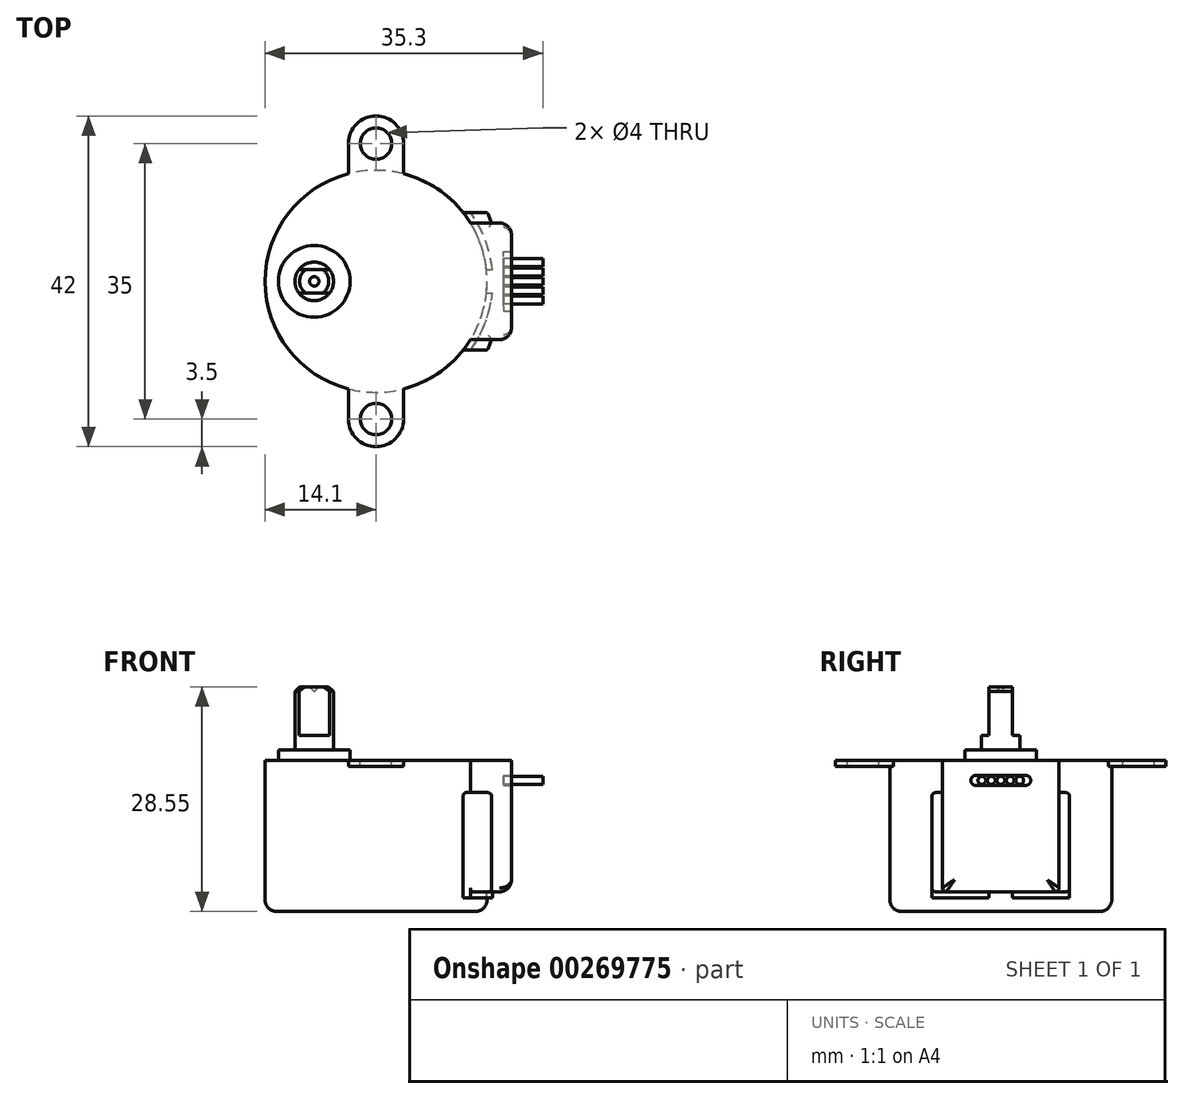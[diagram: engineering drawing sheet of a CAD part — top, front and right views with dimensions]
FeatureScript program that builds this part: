
annotation { "Feature Type Name" : "Feature", "Feature Type Description" : "" }
export const myFeature = defineFeature(function(context is Context, id is Id, definition is map)
    precondition{}
    {
        {
            var Q0;
            Q0=qCreatedBy(makeId("Front.planeOp"),FACE);
            var sketch = newSketch(context, id + "F0", { "sketchPlane" : qUnion([Q0])});
            skLineSegment(sketch, "E0", {"start": v(0, 0) * mm, "end": v(0, 8.75) * mm});
            skLineSegment(sketch, "E1", {"start": v(0.6, 9.35) * mm, "end": v(1.85, 9.35) * mm});
            skLineSegment(sketch, "E2", {"start": v(2.45, 8.75) * mm, "end": v(2.45, 1.35) * mm});
            skLineSegment(sketch, "E3", {"start": v(2.45, 1.35) * mm, "end": v(4.55, 1.35) * mm});
            skLineSegment(sketch, "E4", {"start": v(4.55, 1.35) * mm, "end": v(4.55, 0) * mm});
            skLineSegment(sketch, "E5", {"start": v(4.55, 0) * mm, "end": v(0, 0) * mm});
            skLineSegment(sketch, "E6", {"start": v(1.85, 9.35) * mm, "end": v(2.45, 8.75) * mm});
            skLineSegment(sketch, "E7", {"start": v(0.6, 9.35) * mm, "end": v(0, 8.75) * mm});
            skLineSegment(sketch, "E8", {"start": v(0, 8.75) * mm, "end": v(0, 13.35) * mm, "construction": true});
            skSolve(sketch);
        }
        {
            var Q0;
            Q0=makeQuery(id+"F0.imprint","IMPRINT",FACE,{"disambiguationData":[TD([[makeQuery(id+"F0.imprint","IMPRINT",EDGE,{"derivedFrom":sQuery(id+"F0.wireOp",EDGE,"E0")}),-1.0]])]});
            var Q1;
            Q1=sQuery(id+"F0.wireOp",EDGE,"E8");
            revolve(context, id + "F1", {"entities" : qUnion([Q0]), "axis" : qUnion([Q1]), "revolveType" : RevolveType.FULL});
        }
        {
            var Q0;
            Q0=makeQuery(id+"F1.opRevolve","SWEPT_FACE",FACE,{"disambiguationData":[OSD([sQuery(id+"F0.wireOp",EDGE,"E1")])]});
            var sketch = newSketch(context, id + "F2", { "sketchPlane" : qUnion([Q0])});
            skLineSegment(sketch, "E9", {"start": v(-3.37, 1.5) * mm, "end": v(3.8, 1.5) * mm});
            skLineSegment(sketch, "E10", {"start": v(3.8, 1.5) * mm, "end": v(3.8, 4.5) * mm});
            skLineSegment(sketch, "E11", {"start": v(3.8, 4.5) * mm, "end": v(-3.37, 4.5) * mm});
            skLineSegment(sketch, "E12", {"start": v(-3.37, 4.5) * mm, "end": v(-3.37, 1.5) * mm});
            skLineSegment(sketch, "E13", {"start": v(0, 0) * mm, "end": v(9.16, 0) * mm, "construction": true});
            skLineSegment(sketch, "E14.MirrorCS", {"start": v(-3.37, -4.5) * mm, "end": v(-3.37, -1.5) * mm});
            skLineSegment(sketch, "E15.MirrorCS", {"start": v(3.8, -4.5) * mm, "end": v(-3.37, -4.5) * mm});
            skLineSegment(sketch, "E16.MirrorCS", {"start": v(3.8, -1.5) * mm, "end": v(3.8, -4.5) * mm});
            skLineSegment(sketch, "E17.MirrorCS", {"start": v(-3.37, -1.5) * mm, "end": v(3.8, -1.5) * mm});
            skSolve(sketch);
        }
        {
            var Q0;
            Q0=qSketchRegion(id+"F2",true);
            extrude(context, id + "F3", {"entities" : qUnion([Q0]), "operationType" : NewBodyOperationType.REMOVE, "oppositeDirection" : true, "depth" : 6.2 * mm});
        }
        {
            var Q0;
            Q0=makeQuery(id+"F1.opRevolve","SWEPT_FACE",FACE,{"disambiguationData":[OSD([sQuery(id+"F0.wireOp",EDGE,"E5")])]});
            var sketch = newSketch(context, id + "F4", { "sketchPlane" : qUnion([Q0])});
            skLineSegment(sketch, "E18", {"start": v(0, 0) * mm, "end": v(7.85, 0) * mm, "construction": true});
            skCircle(sketch, "E19", {"center": v(7.85, 0) * mm, "radius": 14.1 * mm});
            skLineSegment(sketch, "E20", {"start": v(0, 0) * mm, "end": v(-4.55, 0) * mm, "construction": true});
            skLineSegment(sketch, "E21", {"start": v(-4.55, 0) * mm, "end": v(-6.25, 0) * mm, "construction": true});
            skSolve(sketch);
        }
        {
            var Q0;
            Q0=qSketchRegion(id+"F4",true);
            extrude(context, id + "F5", {"entities" : qUnion([Q0]), "depth" : 19.2 * mm});
        }
        {
            var Q0;
            Q0=makeQuery(id+"F5.opExtrude","CAP_FACE",FACE,{"disambiguationData":[OSD([sQuery(id+"F0.wireOp",EDGE,"E4"),sQuery(id+"F0.wireOp",EDGE,"E5"),sQuery(id+"F4.wireOp",EDGE,"E19")])],"isStart":true});
            var sketch = newSketch(context, id + "F6", { "sketchPlane" : qUnion([Q0])});
            skLineSegment(sketch, "E22", {"start": v(7.85, 0) * mm, "end": v(7.85, 17.5) * mm, "construction": true});
            skCircle(sketch, "E23", {"center": v(7.85, 17.5) * mm, "radius": 2 * mm});
            skArc(sketch, "E24", {"start": v(11.35, 17.5) * mm, "mid": v(7.85, 21) * mm, "end": v(4.35, 17.5) * mm});
            skLineSegment(sketch, "E25", {"start": v(7.85, 0) * mm, "end": v(11.35, 0) * mm, "construction": true});
            skLineSegment(sketch, "E26", {"start": v(11.35, 0) * mm, "end": v(11.35, 17.5) * mm});
            skLineSegment(sketch, "E27", {"start": v(7.85, 0) * mm, "end": v(4.35, 0) * mm, "construction": true});
            skLineSegment(sketch, "E28", {"start": v(4.35, 0) * mm, "end": v(4.35, 17.5) * mm});
            skLineSegment(sketch, "E29.MirrorCS", {"start": v(4.35, 0) * mm, "end": v(4.35, -17.5) * mm});
            skArc(sketch, "E30.MirrorCS", {"start": v(11.35, -17.5) * mm, "mid": v(7.85, -21) * mm, "end": v(4.35, -17.5) * mm});
            skCircle(sketch, "E31.MirrorC", {"center": v(7.85, -17.5) * mm, "radius": 2 * mm});
            skLineSegment(sketch, "E32.MirrorCS", {"start": v(11.35, 0) * mm, "end": v(11.35, -17.5) * mm});
            skSolve(sketch);
        }
        {
            var Q0;
            Q0=qSketchRegion(id+"F6",true);
            extrude(context, id + "F7", {"entities" : qUnion([Q0]), "oppositeDirection" : true, "depth" : 0.75 * mm});
        }
        {
            var Q0;
            Q0=makeQuery(id+"F7.opExtrude","SWEPT_BODY",BODY,{"disambiguationData":[OSD([sQuery(id+"F6.wireOp",EDGE,"E23"),sQuery(id+"F6.wireOp",EDGE,"E24"),sQuery(id+"F6.wireOp",EDGE,"E26"),sQuery(id+"F6.wireOp",EDGE,"E28"),sQuery(id+"F6.wireOp",EDGE,"E29.MirrorCS"),sQuery(id+"F6.wireOp",EDGE,"E32.MirrorCS"),sQuery(id+"F6.wireOp",EDGE,"E30.MirrorCS"),sQuery(id+"F6.wireOp",EDGE,"E31.MirrorC")])]});
            var Q1;
            Q1=makeQuery(id+"F5.opExtrude","SWEPT_BODY",BODY,{"disambiguationData":[OSD([sQuery(id+"F0.wireOp",EDGE,"E4"),sQuery(id+"F0.wireOp",EDGE,"E5"),sQuery(id+"F4.wireOp",EDGE,"E19")])]});
            booleanBodies(context, id + "F8", {"operationType" : BooleanOperationType.UNION, "tools" : qUnion([Q0, Q1])});
        }
        {
            var Q0;
            Q0=makeQuery(id+"F8.opBoolean","MERGE",FACE,{"derivedFrom":[makeQuery(id+"F5.opExtrude","CAP_FACE",FACE,{"disambiguationData":[OSD([sQuery(id+"F4.wireOp",EDGE,"E19")])],"isStart":true}),makeQuery(id+"F7.opExtrude","CAP_FACE",FACE,{"disambiguationData":[OSD([sQuery(id+"F6.wireOp",EDGE,"E23"),sQuery(id+"F6.wireOp",EDGE,"E24"),sQuery(id+"F6.wireOp",EDGE,"E26"),sQuery(id+"F6.wireOp",EDGE,"E28"),sQuery(id+"F6.wireOp",EDGE,"E29.MirrorCS"),sQuery(id+"F6.wireOp",EDGE,"E32.MirrorCS"),sQuery(id+"F6.wireOp",EDGE,"E30.MirrorCS"),sQuery(id+"F6.wireOp",EDGE,"E31.MirrorC")])],"isStart":true})]});
            var sketch = newSketch(context, id + "F9", { "sketchPlane" : qUnion([Q0])});
            skLineSegment(sketch, "E33", {"start": v(7.85, 0) * mm, "end": v(25.05, 0) * mm, "construction": true});
            skPoint(sketch, "E33.endSnap0", {"position": v(21.95, 0) * mm});
            skLineSegment(sketch, "E34", {"start": v(25.05, 0) * mm, "end": v(25.05, 7.4) * mm});
            skLineSegment(sketch, "E35", {"start": v(25.05, 7.4) * mm, "end": v(7.85, 7.4) * mm});
            skLineSegment(sketch, "E36", {"start": v(7.85, 7.4) * mm, "end": v(7.85, 0) * mm});
            skLineSegment(sketch, "E37.MirrorCS", {"start": v(7.85, -7.4) * mm, "end": v(7.85, 0) * mm});
            skLineSegment(sketch, "E38.MirrorCS", {"start": v(25.05, -7.4) * mm, "end": v(7.85, -7.4) * mm});
            skLineSegment(sketch, "E39.MirrorCS", {"start": v(25.05, 0) * mm, "end": v(25.05, -7.4) * mm});
            skSolve(sketch);
        }
        {
            var Q0;
            {var subQ1=sQuery(id+"F9.wireOp",EDGE,"E34");Q0=makeQuery(id+"F9.imprint","IMPRINT",FACE,{"disambiguationData":[TD([[makeQuery(id+"F9.imprint","IMPRINT",EDGE,{"derivedFrom":subQ1}),1.0]])]});}
            extrude(context, id + "F10", {"entities" : qUnion([Q0]), "operationType" : NewBodyOperationType.ADD, "oppositeDirection" : true, "depth" : 16.7 * mm});
        }
        {
            var Q0;
            Q0=makeQuery(id+"F10.opExtrude","CAP_FACE",FACE,{"disambiguationData":[OSD([sQuery(id+"F4.wireOp",EDGE,"E19"),sQuery(id+"F9.wireOp",EDGE,"E34"),sQuery(id+"F9.wireOp",EDGE,"E35"),sQuery(id+"F9.wireOp",EDGE,"E38.MirrorCS"),sQuery(id+"F9.wireOp",EDGE,"E39.MirrorCS")])],"isStart":false});
            var sketch = newSketch(context, id + "F11", { "sketchPlane" : qUnion([Q0])});
            skLineSegment(sketch, "E40", {"start": v(25.05, 0) * mm, "end": v(21.95, 0) * mm, "construction": true});
            skLineSegment(sketch, "E41", {"start": v(22.55, 0) * mm, "end": v(22.55, 7.4) * mm});
            skLineSegment(sketch, "E42", {"start": v(22.55, 7.4) * mm, "end": v(22.05, 8.75) * mm});
            skLineSegment(sketch, "E43", {"start": v(22.05, 8.75) * mm, "end": v(18.9, 8.75) * mm});
            skLineSegment(sketch, "E44", {"start": v(18.9, 8.75) * mm, "end": v(18.9, 0) * mm});
            skLineSegment(sketch, "E45.MirrorCS", {"start": v(22.55, 0) * mm, "end": v(22.55, -7.4) * mm});
            skLineSegment(sketch, "E46.MirrorCS", {"start": v(22.55, -7.4) * mm, "end": v(22.05, -8.75) * mm});
            skLineSegment(sketch, "E47.MirrorCS", {"start": v(22.05, -8.75) * mm, "end": v(18.9, -8.75) * mm});
            skLineSegment(sketch, "E48.MirrorCS", {"start": v(18.9, -8.75) * mm, "end": v(18.9, 0) * mm});
            skSolve(sketch);
        }
        {
            var Q0;
            {var subQ3=sQuery(id+"F11.wireOp",EDGE,"E42");Q0=makeQuery(id+"F11.imprint","IMPRINT",FACE,{"disambiguationData":[TD([[makeQuery(id+"F11.imprint","IMPRINT",EDGE,{"derivedFrom":subQ3}),1.0]])]});}
            var Q1;
            {var subQ3=sQuery(id+"F11.wireOp",EDGE,"E41");Q1=makeQuery(id+"F11.imprint","IMPRINT",FACE,{"disambiguationData":[TD([[makeQuery(id+"F11.imprint","IMPRINT",EDGE,{"derivedFrom":subQ3}),1.0]])]});}
            extrude(context, id + "F12", {"entities" : qUnion([Q0, Q1]), "operationType" : NewBodyOperationType.ADD, "oppositeDirection" : true, "depth" : 12.6 * mm});
        }
        {
            var Q0;
            Q0=makeQuery(id+"F12.boolean.opBoolean","MERGE",FACE,{"derivedFrom":[makeQuery(id+"F10.opExtrude","CAP_FACE",FACE,{"disambiguationData":[OSD([sQuery(id+"F4.wireOp",EDGE,"E19"),sQuery(id+"F9.wireOp",EDGE,"E34"),sQuery(id+"F9.wireOp",EDGE,"E35"),sQuery(id+"F9.wireOp",EDGE,"E38.MirrorCS"),sQuery(id+"F9.wireOp",EDGE,"E39.MirrorCS")])],"isStart":false}),makeQuery(id+"F12.opExtrude","CAP_FACE",FACE,{"disambiguationData":[OSD([sQuery(id+"F11.wireOp",EDGE,"E41"),sQuery(id+"F11.wireOp",EDGE,"E42"),sQuery(id+"F11.wireOp",EDGE,"E43"),sQuery(id+"F11.wireOp",EDGE,"E44"),sQuery(id+"F11.wireOp",EDGE,"E45.MirrorCS"),sQuery(id+"F11.wireOp",EDGE,"E46.MirrorCS"),sQuery(id+"F11.wireOp",EDGE,"E47.MirrorCS"),sQuery(id+"F11.wireOp",EDGE,"E48.MirrorCS")])],"isStart":true})]});
            var sketch = newSketch(context, id + "F13", { "sketchPlane" : qUnion([Q0])});
            skLineSegment(sketch, "E49", {"start": v(25.05, 0) * mm, "end": v(7.85, 0) * mm, "construction": true});
            skArc(sketch, "E50", {"start": v(18.9, -8.75) * mm, "mid": v(20.9, -5.33) * mm, "end": v(21.87, -1.5) * mm});
            skArc(sketch, "E51", {"start": v(19.84, -8.75) * mm, "mid": v(21.71, -5.3) * mm, "end": v(22.62, -1.5) * mm});
            skLineSegment(sketch, "E52", {"start": v(18.9, -8.75) * mm, "end": v(19.84, -8.75) * mm});
            skLineSegment(sketch, "E53", {"start": v(21.87, -1.5) * mm, "end": v(22.62, -1.5) * mm});
            skLineSegment(sketch, "E54.MirrorCS", {"start": v(21.87, 1.5) * mm, "end": v(22.62, 1.5) * mm});
            skArc(sketch, "E55.MirrorCS", {"start": v(19.84, 8.75) * mm, "mid": v(21.71, 5.3) * mm, "end": v(22.62, 1.5) * mm});
            skArc(sketch, "E56.MirrorCS", {"start": v(18.9, 8.75) * mm, "mid": v(20.9, 5.33) * mm, "end": v(21.87, 1.5) * mm});
            skLineSegment(sketch, "E57.MirrorCS", {"start": v(18.9, 8.75) * mm, "end": v(19.84, 8.75) * mm});
            skSolve(sketch);
        }
        {
            var Q0;
            Q0=makeQuery(id+"F13.imprint","IMPRINT",FACE,{"disambiguationData":[TD([[makeQuery(id+"F13.imprint","IMPRINT",EDGE,{"derivedFrom":sQuery(id+"F13.wireOp",EDGE,"E50")}),-1.0]])]});
            var Q1;
            Q1=makeQuery(id+"F13.imprint","IMPRINT",FACE,{"disambiguationData":[TD([[makeQuery(id+"F13.imprint","IMPRINT",EDGE,{"derivedFrom":sQuery(id+"F13.wireOp",EDGE,"E54.MirrorCS")}),1.0]])]});
            extrude(context, id + "F14", {"entities" : qUnion([Q0, Q1]), "operationType" : NewBodyOperationType.ADD, "depth" : 0.75 * mm});
        }
        {
            var Q0;
            Q0=makeQuery(id+"F10.opExtrude","SWEPT_EDGE",EDGE,{"disambiguationData":[OSD([sQuery(id+"F9.wireOp",EDGE,"E38.MirrorCS"),sQuery(id+"F9.wireOp",EDGE,"E39.MirrorCS")])]});
            var Q1;
            Q1=makeQuery(id+"F10.opExtrude","SWEPT_EDGE",EDGE,{"disambiguationData":[OSD([sQuery(id+"F9.wireOp",EDGE,"E34"),sQuery(id+"F9.wireOp",EDGE,"E35")])]});
            var Q2;
            Q2=makeQuery(id+"F10.opExtrude","CAP_EDGE",EDGE,{"disambiguationData":[OSD([sQuery(id+"F9.wireOp",EDGE,"E34"),sQuery(id+"F9.wireOp",EDGE,"E39.MirrorCS")])],"isStart":false});
            var Q3;
            Q3=makeQuery(id+"F5.opExtrude","CAP_EDGE",EDGE,{"disambiguationData":[OSD([sQuery(id+"F4.wireOp",EDGE,"E19")])],"isStart":false});
            fillet(context, id + "F15", {"entities" : qUnion([Q0, Q1, Q2, Q3]), "radius" : 1.5 * mm, "tangentPropagation" : true, "allowEdgeOverflow" : false});
        }
        {
            var Q0;
            Q0=makeQuery(id+"F10.opExtrude","CAP_EDGE",EDGE,{"disambiguationData":[OSD([sQuery(id+"F9.wireOp",EDGE,"E35")])],"isStart":false});
            var Q1;
            Q1=makeQuery(id+"F12.opExtrude","CAP_EDGE",EDGE,{"disambiguationData":[OSD([sQuery(id+"F11.wireOp",EDGE,"E46.MirrorCS")])],"isStart":true});
            var Q2;
            Q2=makeQuery(id+"F12.opExtrude","CAP_EDGE",EDGE,{"disambiguationData":[OSD([sQuery(id+"F11.wireOp",EDGE,"E47.MirrorCS")])],"isStart":true});
            var Q3;
            Q3=makeQuery(id+"F12.opExtrude","SWEPT_EDGE",EDGE,{"disambiguationData":[OSD([sQuery(id+"F11.wireOp",EDGE,"E46.MirrorCS"),sQuery(id+"F11.wireOp",EDGE,"E47.MirrorCS")])]});
            var Q4;
            Q4=makeQuery(id+"F12.opExtrude","CAP_EDGE",EDGE,{"disambiguationData":[OSD([sQuery(id+"F11.wireOp",EDGE,"E46.MirrorCS")])],"isStart":false});
            var Q5;
            Q5=makeQuery(id+"F12.opExtrude","CAP_EDGE",EDGE,{"disambiguationData":[OSD([sQuery(id+"F11.wireOp",EDGE,"E47.MirrorCS")])],"isStart":false});
            var Q6;
            Q6=makeQuery(id+"F10.opExtrude","CAP_EDGE",EDGE,{"disambiguationData":[OSD([sQuery(id+"F9.wireOp",EDGE,"E38.MirrorCS")])],"isStart":false});
            var Q7;
            Q7=makeQuery(id+"F12.opExtrude","CAP_EDGE",EDGE,{"disambiguationData":[OSD([sQuery(id+"F11.wireOp",EDGE,"E42")])],"isStart":true});
            var Q8;
            Q8=makeQuery(id+"F12.opExtrude","CAP_EDGE",EDGE,{"disambiguationData":[OSD([sQuery(id+"F11.wireOp",EDGE,"E43")])],"isStart":true});
            var Q9;
            Q9=makeQuery(id+"F12.opExtrude","SWEPT_EDGE",EDGE,{"disambiguationData":[OSD([sQuery(id+"F11.wireOp",EDGE,"E42"),sQuery(id+"F11.wireOp",EDGE,"E43")])]});
            var Q10;
            Q10=makeQuery(id+"F12.opExtrude","CAP_EDGE",EDGE,{"disambiguationData":[OSD([sQuery(id+"F11.wireOp",EDGE,"E42")])],"isStart":false});
            var Q11;
            Q11=makeQuery(id+"F12.opExtrude","CAP_EDGE",EDGE,{"disambiguationData":[OSD([sQuery(id+"F11.wireOp",EDGE,"E43")])],"isStart":false});
            fillet(context, id + "F16", {"entities" : qUnion([Q0, Q1, Q2, Q3, Q4, Q5, Q6, Q7, Q8, Q9, Q10, Q11]), "radius" : 0.5 * mm, "tangentPropagation" : true, "allowEdgeOverflow" : false});
        }
        {
            var Q0;
            Q0=makeQuery(id+"F10.opExtrude","SWEPT_FACE",FACE,{"disambiguationData":[OSD([sQuery(id+"F9.wireOp",EDGE,"E34"),sQuery(id+"F9.wireOp",EDGE,"E39.MirrorCS")])]});
            var sketch = newSketch(context, id + "F17", { "sketchPlane" : qUnion([Q0])});
            skLineSegment(sketch, "E58", {"start": v(0, 0) * mm, "end": v(0, -2.55) * mm, "construction": true});
            skLineSegment(sketch, "E59", {"start": v(0, -2.55) * mm, "end": v(-3.15, -2.55) * mm, "construction": true});
            skArc(sketch, "E60", {"start": v(-3.15, -1.9) * mm, "mid": v(-3.8, -2.55) * mm, "end": v(-3.15, -3.2) * mm});
            skLineSegment(sketch, "E61", {"start": v(-3.15, -1.9) * mm, "end": v(0, -1.9) * mm});
            skPoint(sketch, "E61.endSnap0", {"position": v(0, -1.27) * mm});
            skLineSegment(sketch, "E62", {"start": v(-3.15, -3.2) * mm, "end": v(0, -3.2) * mm});
            skLineSegment(sketch, "E63.MirrorCS", {"start": v(3.15, -1.9) * mm, "end": v(0, -1.9) * mm});
            skArc(sketch, "E64.MirrorCS", {"start": v(3.15, -1.9) * mm, "mid": v(3.8, -2.55) * mm, "end": v(3.15, -3.2) * mm});
            skLineSegment(sketch, "E65.MirrorCS", {"start": v(3.15, -3.2) * mm, "end": v(0, -3.2) * mm});
            skSolve(sketch);
        }
        {
            var Q0;
            Q0=makeQuery(id+"F17.imprint","IMPRINT",FACE,{"disambiguationData":[TD([[makeQuery(id+"F17.imprint","IMPRINT",EDGE,{"derivedFrom":sQuery(id+"F17.wireOp",EDGE,"E60")}),1.0]])]});
            extrude(context, id + "F18", {"entities" : qUnion([Q0]), "operationType" : NewBodyOperationType.REMOVE, "oppositeDirection" : true, "depth" : 1 * mm});
        }
        {
            var Q0;
            Q0=makeQuery(id+"F18.boolean.opBoolean","COPY",FACE,{"derivedFrom":makeQuery(id+"F18.opExtrude","CAP_FACE",FACE,{"disambiguationData":[OSD([sQuery(id+"F17.wireOp",EDGE,"E60"),sQuery(id+"F17.wireOp",EDGE,"E61"),sQuery(id+"F17.wireOp",EDGE,"E62"),sQuery(id+"F17.wireOp",EDGE,"E63.MirrorCS"),sQuery(id+"F17.wireOp",EDGE,"E64.MirrorCS"),sQuery(id+"F17.wireOp",EDGE,"E65.MirrorCS")])],"isStart":false})});
            var sketch = newSketch(context, id + "F19", { "sketchPlane" : qUnion([Q0])});
            skLineSegment(sketch, "E66", {"start": v(0, -3.2) * mm, "end": v(0, -1.9) * mm, "construction": true});
            skLineSegment(sketch, "E67", {"start": v(0, -2.55) * mm, "end": v(1.2, -2.55) * mm, "construction": true});
            skLineSegment(sketch, "E68", {"start": v(1.2, -2.55) * mm, "end": v(2.4, -2.55) * mm, "construction": true});
            skLineSegment(sketch, "E69", {"start": v(0, -2.55) * mm, "end": v(-1.2, -2.55) * mm, "construction": true});
            skLineSegment(sketch, "E70", {"start": v(-1.2, -2.55) * mm, "end": v(-2.4, -2.55) * mm, "construction": true});
            skCircle(sketch, "E71", {"center": v(0, -2.55) * mm, "radius": 0.5 * mm});
            skCircle(sketch, "E72", {"center": v(-1.2, -2.55) * mm, "radius": 0.5 * mm});
            skCircle(sketch, "E73", {"center": v(-2.4, -2.55) * mm, "radius": 0.5 * mm});
            skCircle(sketch, "E74", {"center": v(1.2, -2.55) * mm, "radius": 0.5 * mm});
            skCircle(sketch, "E75", {"center": v(2.4, -2.55) * mm, "radius": 0.5 * mm});
            skSolve(sketch);
        }
        {
            var Q0;
            Q0=makeQuery(id+"F19.imprint","IMPRINT",FACE,{"disambiguationData":[TD([[makeQuery(id+"F19.imprint","IMPRINT",EDGE,{"derivedFrom":sQuery(id+"F19.wireOp",EDGE,"E73")}),1.0]])]});
            extrude(context, id + "F20", {"entities" : qUnion([Q0]), "depth" : 5 * mm});
        }
        {
            var Q0;
            Q0=makeQuery(id+"F19.imprint","IMPRINT",FACE,{"disambiguationData":[TD([[makeQuery(id+"F19.imprint","IMPRINT",EDGE,{"derivedFrom":sQuery(id+"F19.wireOp",EDGE,"E72")}),1.0]])]});
            extrude(context, id + "F21", {"entities" : qUnion([Q0]), "depth" : 5 * mm});
        }
        {
            var Q0;
            Q0=makeQuery(id+"F19.imprint","IMPRINT",FACE,{"disambiguationData":[TD([[makeQuery(id+"F19.imprint","IMPRINT",EDGE,{"derivedFrom":sQuery(id+"F19.wireOp",EDGE,"E71")}),1.0]])]});
            extrude(context, id + "F22", {"entities" : qUnion([Q0]), "depth" : 5 * mm});
        }
        {
            var Q0;
            Q0=makeQuery(id+"F19.imprint","IMPRINT",FACE,{"disambiguationData":[TD([[makeQuery(id+"F19.imprint","IMPRINT",EDGE,{"derivedFrom":sQuery(id+"F19.wireOp",EDGE,"E74")}),1.0]])]});
            extrude(context, id + "F23", {"entities" : qUnion([Q0]), "depth" : 5 * mm});
        }
        {
            var Q0;
            Q0=makeQuery(id+"F19.imprint","IMPRINT",FACE,{"disambiguationData":[TD([[makeQuery(id+"F19.imprint","IMPRINT",EDGE,{"derivedFrom":sQuery(id+"F19.wireOp",EDGE,"E75")}),1.0]])]});
            extrude(context, id + "F24", {"entities" : qUnion([Q0]), "depth" : 5 * mm});
        }
    });
